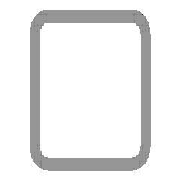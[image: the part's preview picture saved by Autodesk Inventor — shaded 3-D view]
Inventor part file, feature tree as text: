
AUTODESK INVENTOR PART (.ipt)
format: ipt  version: 2022 (Build 260153000, 153)  size: 248,320 bytes
history: native  units: mm (DEFAULTED — no unit token found)
features: other x7, sketch x3, surface_op x2, plane x1
ambient origin geometry x8: Origin, YZ Plane, XZ Plane, XY Plane, X Axis, Y Axis, Z Axis, Center Point
bodies: Solid1 (feature_tree), Body (feature_tree), Solid3 (feature_tree)
feature tree (13):
  parser-record x1  (decoder bookkeeping rows leaked as tree rows — omitted from the tree; the rows remain in map.json)
  other  "Driven Length"
  other  "Start Plane"
  other  "End Plane"
  sketch  "Sketch"  dims[d7=8.0mm d9=40.0mm d11=40.0mm d12=4.0mm d13=-0.0mm d14=180.0mm d15=20.0mm d16=20.0mm d17=90.0deg d18=180.0mm d37=5.0mm d38=5.0mm d39=5.0mm d40=5.0mm d41=5.0mm d42=5.0mm d43=5.0mm d44=5.0mm d45=0.0mm d46=5.0mm d47=5.0mm d48=5.0mm d49=5.0mm d50=5.0mm d51=5.0mm d52=5.0mm d53=5.0mm d54=0.0mm]
  sketch  "Sketch3"  dims[d3=156.0mm]
  plane  "Work Plane3"
  sketch  "Sketch4"  dims[d4=0.0mm]
  other  "Srf5"
  other  "Srf6"
  other  "Srf4"
  surface_op  "Boundary Patch3"
  surface_op  "Boundary Patch4"
